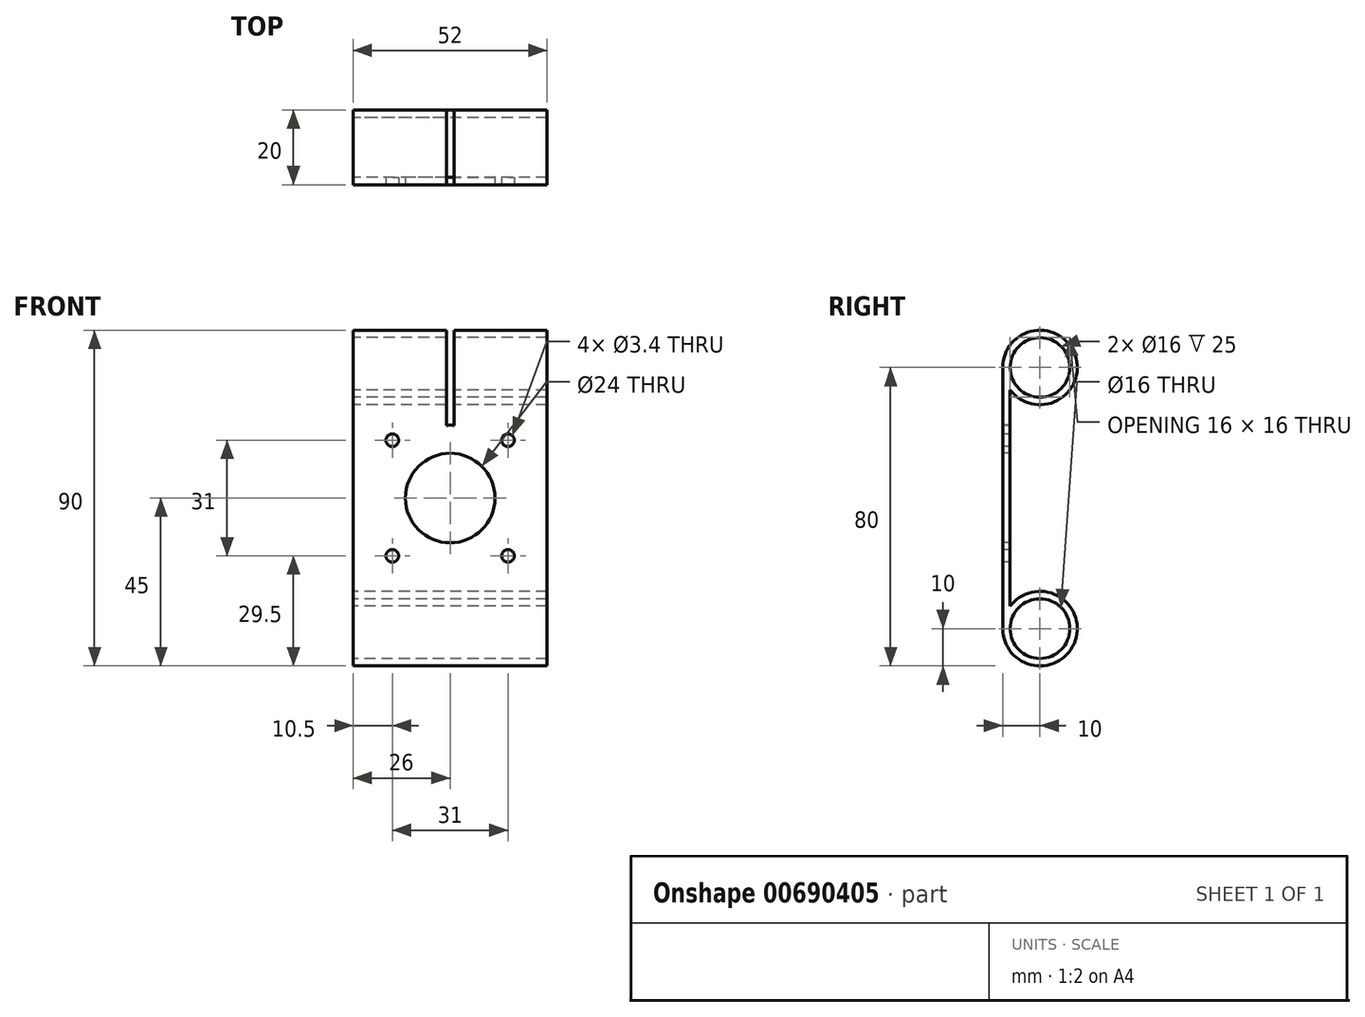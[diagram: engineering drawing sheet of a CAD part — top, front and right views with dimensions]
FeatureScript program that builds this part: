
annotation { "Feature Type Name" : "Feature", "Feature Type Description" : "" }
export const myFeature = defineFeature(function(context is Context, id is Id, definition is map)
    precondition{}
    {
        {
            var Q0;
            Q0=qCreatedBy(makeId("Right.planeOp"),FACE);
            var sketch = newSketch(context, id + "F0", { "sketchPlane" : qUnion([Q0])});
            skLineSegment(sketch, "E0", {"start": v(0, 35) * mm, "end": v(0, -35) * mm});
            skArc(sketch, "E1", {"start": v(2, 29) * mm, "mid": v(19.49, 38.16) * mm, "end": v(0, 35) * mm});
            skArc(sketch, "E2", {"start": v(0, -35) * mm, "mid": v(19.49, -38.16) * mm, "end": v(2, -29) * mm});
            skLineSegment(sketch, "E3", {"start": v(2, 29) * mm, "end": v(2, -29) * mm});
            skCircle(sketch, "E4", {"center": v(10, 35) * mm, "radius": 8 * mm});
            skCircle(sketch, "E5", {"center": v(10, -35) * mm, "radius": 8 * mm});
            skPoint(sketch, "E6.orphan", {"position": v(2, 35) * mm});
            skPoint(sketch, "E7.orphan", {"position": v(2, -35) * mm});
            skLineSegment(sketch, "E8", {"start": v(10, 25) * mm, "end": v(10, -25) * mm, "construction": true});
            skSolve(sketch);
        }
        {
            var Q0;
            Q0 = qSketchRegion(id + "F0", true);
            extrude(context, id + "F1", {"entities" : qUnion([Q0]), "endBound" : BoundingType.SYMMETRIC, "depth" : 52 * mm, "offsetDistance" : 25 * mm});
        }
        {
            var Q0;
            Q0=makeQuery(id+"F1.opExtrude","SWEPT_FACE",FACE,{"disambiguationData":[OSD([sQuery(id+"F0.wireOp",EDGE,"E0")])]});
            var sketch = newSketch(context, id + "F2", { "sketchPlane" : qUnion([Q0])});
            skCircle(sketch, "E9", {"center": v(0, 0) * mm, "radius": 12 * mm});
            skLineSegment(sketch, "E10.bottom", {"start": v(15.5, 15.5) * mm, "end": v(-15.5, 15.5) * mm, "construction": true});
            skLineSegment(sketch, "E10.top", {"start": v(15.5, -15.5) * mm, "end": v(-15.5, -15.5) * mm, "construction": true});
            skLineSegment(sketch, "E10.left", {"start": v(15.5, 15.5) * mm, "end": v(15.5, -15.5) * mm, "construction": true});
            skLineSegment(sketch, "E10.right", {"start": v(-15.5, 15.5) * mm, "end": v(-15.5, -15.5) * mm, "construction": true});
            skLineSegment(sketch, "E11", {"start": v(0, 15.5) * mm, "end": v(0, -15.5) * mm, "construction": true});
            skCircle(sketch, "E12", {"center": v(-15.5, 15.5) * mm, "radius": 1.7 * mm});
            skCircle(sketch, "E13", {"center": v(15.5, 15.5) * mm, "radius": 1.7 * mm});
            skCircle(sketch, "E14", {"center": v(15.5, -15.5) * mm, "radius": 1.7 * mm});
            skCircle(sketch, "E15", {"center": v(-15.5, -15.5) * mm, "radius": 1.7 * mm});
            skSolve(sketch);
        }
        {
            var Q0;
            Q0 = qSketchRegion(id + "F2", true);
            extrude(context, id + "F3", {"entities" : qUnion([Q0]), "operationType" : NewBodyOperationType.REMOVE, "oppositeDirection" : true, "depth" : 25 * mm, "offsetDistance" : 25 * mm});
        }
        {
            var Q0;
            Q0=makeQuery(id+"F1.opExtrude","SWEPT_FACE",FACE,{"disambiguationData":[OSD([sQuery(id+"F0.wireOp",EDGE,"E0")])]});
            var sketch = newSketch(context, id + "F4", { "sketchPlane" : qUnion([Q0])});
            skLineSegment(sketch, "E16.bottom", {"start": v(1, 45) * mm, "end": v(-1, 45) * mm});
            skLineSegment(sketch, "E16.left", {"start": v(1, 45) * mm, "end": v(1, 19.47) * mm});
            skLineSegment(sketch, "E16.right", {"start": v(-1, 45) * mm, "end": v(-1, 19.47) * mm});
            skPoint(sketch, "E16.middle", {"position": v(0, 32.24) * mm});
            skLineSegment(sketch, "E17.0", {"start": v(-26, 45) * mm, "end": v(-26, 25) * mm, "construction": true});
            skArc(sketch, "E18.0", {"start": v(1, 19.47) * mm, "mid": v(0, 19.5) * mm, "end": v(-1, 19.47) * mm});
            skSolve(sketch);
        }
        {
            var Q0;
            Q0 = qSketchRegion(id + "F4", true);
            extrude(context, id + "F5", {"entities" : qUnion([Q0]), "operationType" : NewBodyOperationType.REMOVE, "endBound" : BoundingType.THROUGH_ALL, "oppositeDirection" : true, "depth" : 25 * mm, "offsetDistance" : 25 * mm});
        }
    });
